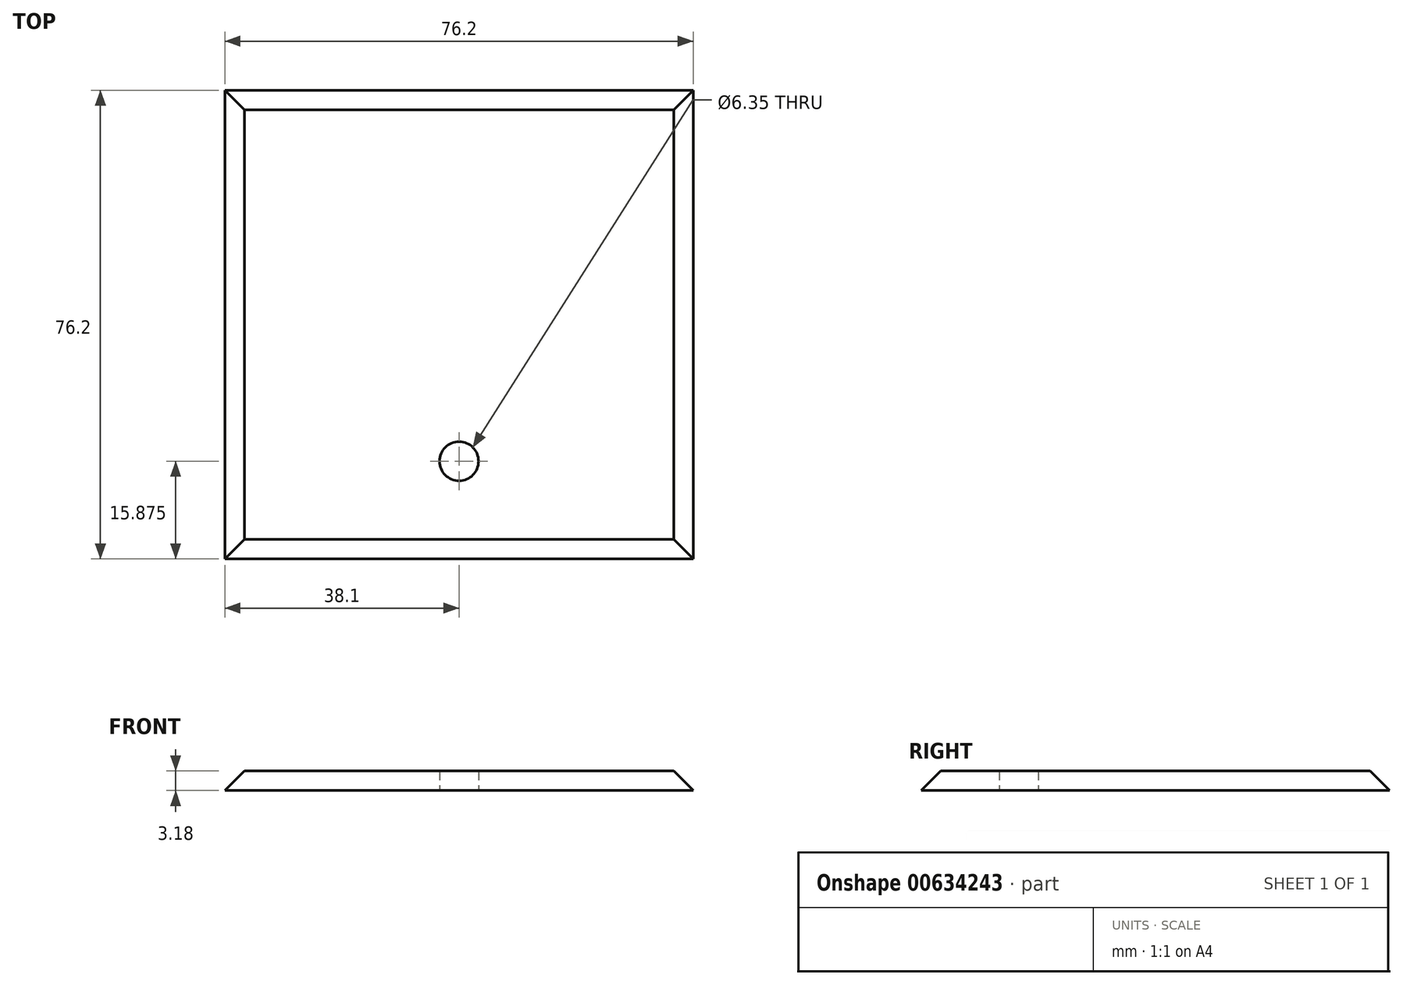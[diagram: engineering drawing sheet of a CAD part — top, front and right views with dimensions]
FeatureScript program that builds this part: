
annotation { "Feature Type Name" : "Feature", "Feature Type Description" : "" }
export const myFeature = defineFeature(function(context is Context, id is Id, definition is map)
    precondition{}
    {
        {
            var Q0;
            Q0=qCreatedBy(makeId("Top.planeOp"),FACE);
            var sketch = newSketch(context, id + "F0", { "sketchPlane" : qUnion([Q0])});
            skLineSegment(sketch, "E0.bottom", {"start": v(0, 0) * mm, "end": v(76.2, 0) * mm});
            skLineSegment(sketch, "E0.top", {"start": v(0, 76.2) * mm, "end": v(76.2, 76.2) * mm});
            skLineSegment(sketch, "E0.left", {"start": v(0, 0) * mm, "end": v(0, 76.2) * mm});
            skLineSegment(sketch, "E0.right", {"start": v(76.2, 0) * mm, "end": v(76.2, 76.2) * mm});
            skCircle(sketch, "E1", {"center": v(38.1, 15.88) * mm, "radius": 3.18 * mm});
            skSolve(sketch);
        }
        {
            var Q0;
            Q0=qSketchRegion(id+"F0",true);
            extrude(context, id + "F1", {"entities" : qUnion([Q0]), "depth" : 3.17 * mm, "offsetDistance" : 25.4 * mm});
        }
        {
            var Q0;
            Q0=makeQuery(id+"F1.opExtrude","CAP_EDGE",EDGE,{"disambiguationData":[OSD([sQuery(id+"F0.wireOp",EDGE,"E0.top")])],"isStart":false});
            var Q1;
            Q1=makeQuery(id+"F1.opExtrude","CAP_EDGE",EDGE,{"disambiguationData":[OSD([sQuery(id+"F0.wireOp",EDGE,"E0.right")])],"isStart":false});
            var Q2;
            Q2=makeQuery(id+"F1.opExtrude","CAP_EDGE",EDGE,{"disambiguationData":[OSD([sQuery(id+"F0.wireOp",EDGE,"E0.bottom")])],"isStart":false});
            var Q3;
            Q3=makeQuery(id+"F1.opExtrude","CAP_EDGE",EDGE,{"disambiguationData":[OSD([sQuery(id+"F0.wireOp",EDGE,"E0.left")])],"isStart":false});
            chamfer(context, id + "F2", {"entities" : qUnion([Q0, Q1, Q2, Q3]), "width" : 3.17 * mm, "tangentPropagation" : true});
        }
    });
